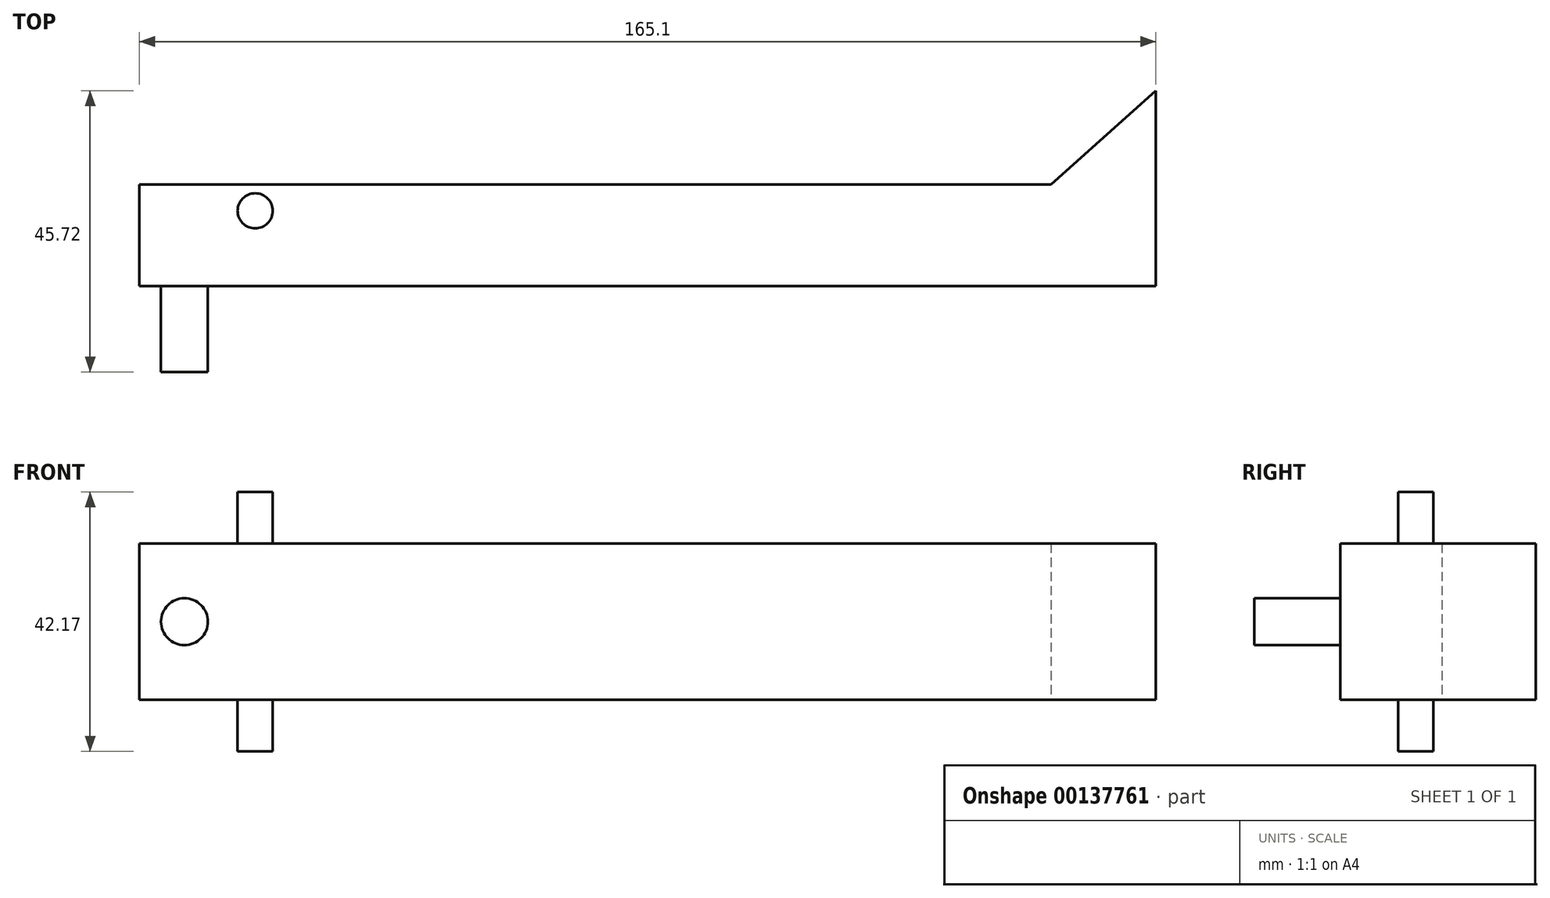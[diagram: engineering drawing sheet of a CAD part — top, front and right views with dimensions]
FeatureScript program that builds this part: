
annotation { "Feature Type Name" : "Feature", "Feature Type Description" : "" }
export const myFeature = defineFeature(function(context is Context, id is Id, definition is map)
    precondition{}
    {
        {
            var Q0;
            Q0=qCreatedBy(makeId("Front.planeOp"),FACE);
            var sketch = newSketch(context, id + "F0", { "sketchPlane" : qUnion([Q0])});
            skLineSegment(sketch, "E0.bottom", {"start": v(-65.26, 14.24) * mm, "end": v(99.84, 14.24) * mm});
            skLineSegment(sketch, "E0.top", {"start": v(-65.26, -11.16) * mm, "end": v(99.84, -11.16) * mm});
            skLineSegment(sketch, "E0.left", {"start": v(-65.26, 14.24) * mm, "end": v(-65.26, -11.16) * mm});
            skLineSegment(sketch, "E0.right", {"start": v(99.84, 14.24) * mm, "end": v(99.84, -11.16) * mm});
            skLineSegment(sketch, "E1", {"start": v(-65.26, 1.54) * mm, "end": v(99.84, 1.54) * mm, "construction": true});
            skSolve(sketch);
        }
        {
            var Q0;
            Q0=makeQuery(id+"F0.imprint","IMPRINT",FACE,{"disambiguationData":[TD([[makeQuery(id+"F0.imprint","IMPRINT",EDGE,{"derivedFrom":sQuery(id+"F0.wireOp",EDGE,"E0.bottom")}),-1.0]])]});
            var Q1;
            Q1=makeQuery(id+"F0.imprint","IMPRINT",FACE,{"disambiguationData":[TD([[makeQuery(id+"F0.imprint","IMPRINT",EDGE,{"derivedFrom":sQuery(id+"F0.wireOp",EDGE,"M2pgWJv9-Swt0-cPwD-kHqv-hG4U1bovwf7z")}),1.0]])]});
            extrude(context, id + "F1", {"entities" : qUnion([Q0, Q1]), "depth" : 16.5 * mm});
        }
        {
            var Q0;
            Q0=makeQuery(id+"F1.opExtrude","CAP_FACE",FACE,{"disambiguationData":[OSD([sQuery(id+"F0.wireOp",EDGE,"E0.bottom"),sQuery(id+"F0.wireOp",EDGE,"E0.top"),sQuery(id+"F0.wireOp",EDGE,"E0.left"),sQuery(id+"F0.wireOp",EDGE,"E0.right")])],"isStart":false});
            var sketch = newSketch(context, id + "F2", { "sketchPlane" : qUnion([Q0])});
            skLineSegment(sketch, "E2", {"start": v(-65.26, 1.54) * mm, "end": v(99.84, 1.54) * mm, "construction": true});
            skCircle(sketch, "E3", {"center": v(-57.95, 1.54) * mm, "radius": 3.81 * mm});
            skSolve(sketch);
        }
        {
            var Q0;
            Q0=qSketchRegion(id+"F2",true);
            extrude(context, id + "F3", {"entities" : qUnion([Q0]), "operationType" : NewBodyOperationType.ADD, "depth" : 13.97 * mm});
        }
        {
            var Q0;
            Q0=makeQuery(id+"F1.opExtrude","SWEPT_FACE",FACE,{"disambiguationData":[OSD([sQuery(id+"F0.wireOp",EDGE,"E0.top")])]});
            var sketch = newSketch(context, id + "F4", { "sketchPlane" : qUnion([Q0])});
            skLineSegment(sketch, "E4", {"start": v(82.8, 0) * mm, "end": v(99.84, 0) * mm});
            skLineSegment(sketch, "E5", {"start": v(99.84, 0) * mm, "end": v(99.84, -15.24) * mm});
            skLineSegment(sketch, "E6", {"start": v(99.84, -15.24) * mm, "end": v(82.8, 0) * mm});
            skSolve(sketch);
        }
        {
            var Q0;
            Q0=makeQuery(id+"F1.opExtrude","SWEPT_FACE",FACE,{"disambiguationData":[OSD([sQuery(id+"F0.wireOp",EDGE,"E0.top")])]});
            var sketch = newSketch(context, id + "F5", { "sketchPlane" : qUnion([Q0])});
            skLineSegment(sketch, "E7", {"start": v(-65.26, 4.28) * mm, "end": v(99.84, 4.28) * mm, "construction": true});
            skCircle(sketch, "E8", {"center": v(-46.46, 4.28) * mm, "radius": 2.86 * mm});
            skSolve(sketch);
        }
        {
            var Q0;
            Q0=qSketchRegion(id+"F5",true);
            extrude(context, id + "F6", {"entities" : qUnion([Q0]), "operationType" : NewBodyOperationType.ADD, "depth" : 8.38 * mm, "hasSecondDirection" : true, "secondDirectionOppositeDirection" : true, "secondDirectionDepth" : 33.78 * mm});
        }
        {
            var Q0;
            Q0=qSketchRegion(id+"F4",true);
            extrude(context, id + "F7", {"entities" : qUnion([Q0]), "operationType" : NewBodyOperationType.ADD, "oppositeDirection" : true, "depth" : 25.4 * mm});
        }
    });
